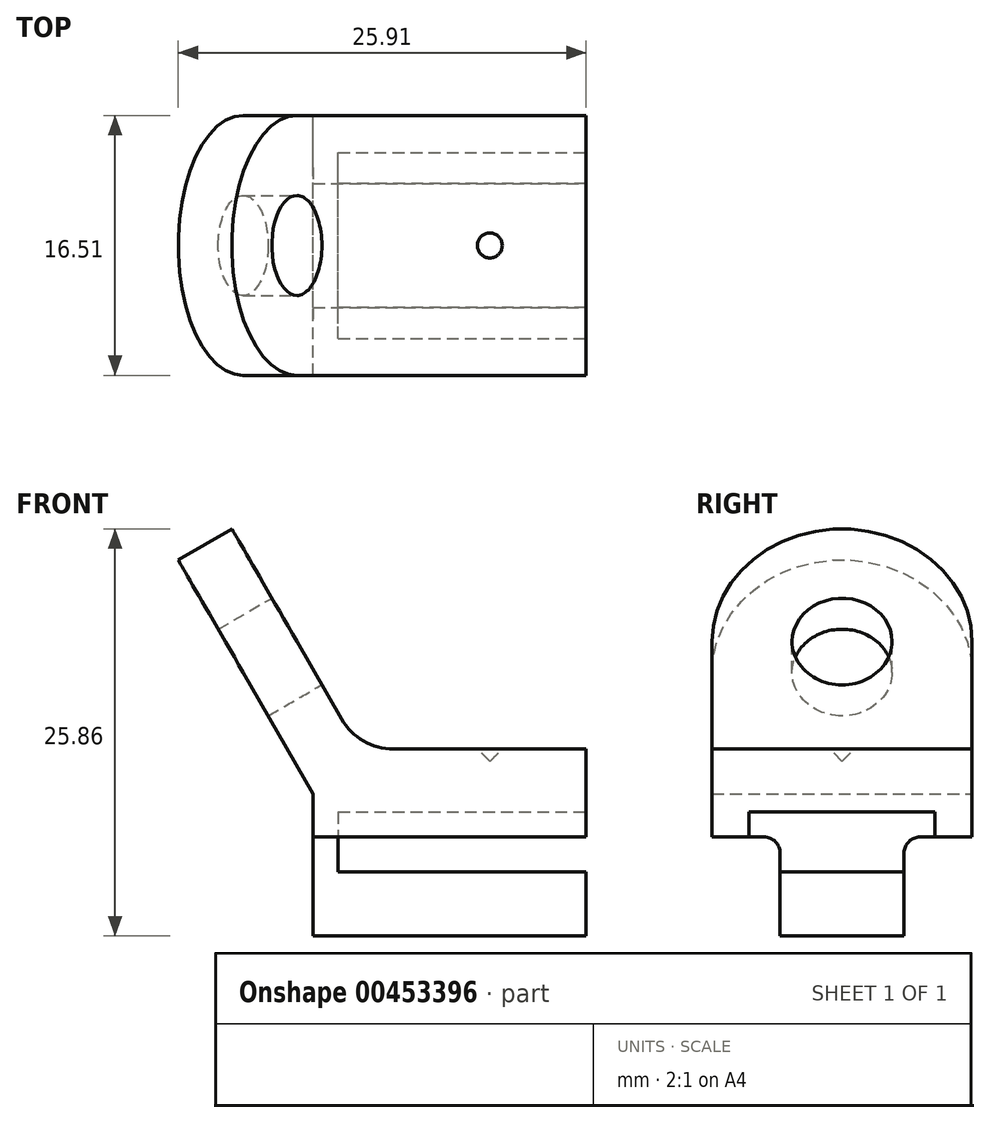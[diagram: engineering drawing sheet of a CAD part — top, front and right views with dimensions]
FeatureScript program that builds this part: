
annotation { "Feature Type Name" : "Feature", "Feature Type Description" : "" }
export const myFeature = defineFeature(function(context is Context, id is Id, definition is map)
    precondition{}
    {
        {
            var Q0;
            Q0=qCreatedBy(makeId("Front.planeOp"),FACE);
            var sketch = newSketch(context, id + "F0", { "sketchPlane" : qUnion([Q0])});
            skLineSegment(sketch, "E0", {"start": v(15.75, 0) * mm, "end": v(0, 0) * mm});
            skLineSegment(sketch, "E1", {"start": v(0, 0) * mm, "end": v(-10.16, 17.6) * mm});
            skLineSegment(sketch, "E2.0", {"start": v(1.32, 5.59) * mm, "end": v(-6.75, 19.57) * mm});
            skLineSegment(sketch, "E3", {"start": v(-10.16, 17.6) * mm, "end": v(-6.75, 19.57) * mm});
            skLineSegment(sketch, "E4", {"start": v(15.75, 5.59) * mm, "end": v(15.75, 0) * mm});
            skLineSegment(sketch, "E5", {"start": v(15.75, 5.59) * mm, "end": v(1.32, 5.59) * mm});
            skSolve(sketch);
        }
        {
            var Q0;
            Q0=makeQuery(id+"F0.imprint","IMPRINT",FACE,{"disambiguationData":[TD([[makeQuery(id+"F0.imprint","IMPRINT",EDGE,{"derivedFrom":sQuery(id+"F0.wireOp",EDGE,"E0")}),-1.0]])]});
            extrude(context, id + "F1", {"entities" : qUnion([Q0]), "depth" : 16.5 * mm});
        }
        {
            var Q0;
            Q0=makeQuery(id+"F1.opExtrude","SWEPT_FACE",FACE,{"disambiguationData":[OSD([sQuery(id+"F0.wireOp",EDGE,"E4")])]});
            var sketch = newSketch(context, id + "F2", { "sketchPlane" : qUnion([Q0])});
            skLineSegment(sketch, "E6.bottom", {"start": v(-2.35, 0) * mm, "end": v(-14.16, 0) * mm});
            skLineSegment(sketch, "E6.top", {"start": v(-2.35, 1.59) * mm, "end": v(-14.16, 1.59) * mm});
            skLineSegment(sketch, "E6.left", {"start": v(-2.35, 0) * mm, "end": v(-2.35, 1.59) * mm});
            skLineSegment(sketch, "E6.right", {"start": v(-14.16, 0) * mm, "end": v(-14.16, 1.59) * mm});
            skPoint(sketch, "E6.middle", {"position": v(-8.26, 0.8) * mm});
            skSolve(sketch);
        }
        {
            var Q0;
            Q0 = qSketchRegion(id + "F2", true);
            extrude(context, id + "F3", {"entities" : qUnion([Q0]), "operationType" : NewBodyOperationType.REMOVE, "endBound" : BoundingType.THROUGH_ALL, "oppositeDirection" : true, "depth" : 12.7 * mm});
        }
        {
            var Q0;
            Q0=makeQuery(id+"F2.imprint","IMPRINT",FACE,{"disambiguationData":[TD([[makeQuery(id+"F2.imprint","IMPRINT",EDGE,{"derivedFrom":sQuery(id+"F2.wireOp",EDGE,"E6.bottom")}),1.0]])]});
            extrude(context, id + "F4", {"entities" : qUnion([Q0]), "operationType" : NewBodyOperationType.REMOVE, "endBound" : BoundingType.THROUGH_ALL, "oppositeDirection" : true, "depth" : 25.4 * mm});
        }
        {
            var Q0;
            Q0=makeQuery(id+"F1.opExtrude","SWEPT_FACE",FACE,{"disambiguationData":[OSD([sQuery(id+"F0.wireOp",EDGE,"E2.0")])]});
            var sketch = newSketch(context, id + "F5", { "sketchPlane" : qUnion([Q0])});
            skCircle(sketch, "E7", {"center": v(-8.26, 12.06) * mm, "radius": 3.18 * mm});
            skSolve(sketch);
        }
        {
            var Q0;
            Q0=makeQuery(id+"F5.imprint","IMPRINT",FACE,{"disambiguationData":[TD([[makeQuery(id+"F5.imprint","IMPRINT",EDGE,{"derivedFrom":sQuery(id+"F5.wireOp",EDGE,"E7")}),1.0]])]});
            extrude(context, id + "F6", {"entities" : qUnion([Q0]), "operationType" : NewBodyOperationType.REMOVE, "endBound" : BoundingType.THROUGH_ALL, "oppositeDirection" : true, "depth" : 25.4 * mm});
        }
        {
            var Q0;
            Q0=makeQuery(id+"F1.opExtrude","CAP_FACE",FACE,{"disambiguationData":[OSD([sQuery(id+"F0.wireOp",EDGE,"E0"),sQuery(id+"F0.wireOp",EDGE,"E1"),sQuery(id+"F0.wireOp",EDGE,"E2.0"),sQuery(id+"F0.wireOp",EDGE,"E3"),sQuery(id+"F0.wireOp",EDGE,"E4"),sQuery(id+"F0.wireOp",EDGE,"E5")])],"isStart":false});
            var Q1;
            Q1=makeQuery(id+"F1.opExtrude","CAP_FACE",FACE,{"disambiguationData":[OSD([sQuery(id+"F0.wireOp",EDGE,"E0"),sQuery(id+"F0.wireOp",EDGE,"E1"),sQuery(id+"F0.wireOp",EDGE,"E2.0"),sQuery(id+"F0.wireOp",EDGE,"E3"),sQuery(id+"F0.wireOp",EDGE,"E4"),sQuery(id+"F0.wireOp",EDGE,"E5")])],"isStart":true});
            cPlane(context, id + "F7", {"entities" : qUnion([Q0, Q1]), "cplaneType" : CPlaneType.MID_PLANE, "offset" : 25.4 * mm, "width" : 152.4 * mm, "height" : 152.4 * mm});
        }
        {
            var Q0;
            Q0=qCreatedBy(id+"F7.planeOp",FACE);
            var sketch = newSketch(context, id + "F8", { "sketchPlane" : qUnion([Q0])});
            skLineSegment(sketch, "E8.0.0", {"start": v(0, 0) * mm, "end": v(-6.47, 11.2) * mm});
            skLineSegment(sketch, "E8.0.1", {"start": v(-6.47, 11.2) * mm, "end": v(-3.06, 13.17) * mm});
            skLineSegment(sketch, "E8.0.2", {"start": v(-3.06, 13.17) * mm, "end": v(1.32, 5.59) * mm});
            skLineSegment(sketch, "E8.0.3", {"start": v(1.32, 5.59) * mm, "end": v(15.75, 5.59) * mm});
            skLineSegment(sketch, "E8.0.4", {"start": v(15.75, 5.59) * mm, "end": v(15.75, 0) * mm});
            skLineSegment(sketch, "E8.0.5", {"start": v(15.75, 0) * mm, "end": v(0, 0) * mm});
            skLineSegment(sketch, "E9", {"start": v(-1.59, 2.75) * mm, "end": v(-1.59, -6.29) * mm});
            skLineSegment(sketch, "E10", {"start": v(-1.59, -6.29) * mm, "end": v(15.75, -6.29) * mm});
            skLineSegment(sketch, "E11", {"start": v(15.75, -6.29) * mm, "end": v(15.75, -2.22) * mm});
            skLineSegment(sketch, "E12", {"start": v(15.75, -2.22) * mm, "end": v(0, -2.22) * mm});
            skLineSegment(sketch, "E13", {"start": v(0, -2.22) * mm, "end": v(0, 0) * mm});
            skLineSegment(sketch, "E14.0", {"start": v(-0.92, 1.59) * mm, "end": v(15.75, 1.59) * mm});
            skSolve(sketch);
        }
        {
            var Q0;
            {var subQ0=sQuery(id+"F8.wireOp",EDGE,"E9");Q0=makeQuery(id+"F8.imprint","IMPRINT",FACE,{"disambiguationData":[TD([[makeQuery(id+"F8.imprint","IMPRINT",EDGE,{"derivedFrom":subQ0}),1.0]])]});}
            extrude(context, id + "F9", {"entities" : qUnion([Q0]), "operationType" : NewBodyOperationType.ADD, "endBound" : BoundingType.SYMMETRIC, "depth" : 7.87 * mm});
        }
        {
            var Q0;
            Q0=qCreatedBy(id+"F7.planeOp",FACE);
            var sketch = newSketch(context, id + "F10", { "sketchPlane" : qUnion([Q0])});
            skLineSegment(sketch, "E15.0.1", {"start": v(0, 0) * mm, "end": v(0, -2.22) * mm});
            skLineSegment(sketch, "E15.0.2", {"start": v(0, -2.22) * mm, "end": v(15.75, -2.22) * mm});
            skLineSegment(sketch, "E15.0.3", {"start": v(15.75, -2.22) * mm, "end": v(15.75, -6.29) * mm});
            skLineSegment(sketch, "E15.0.4", {"start": v(15.75, -6.29) * mm, "end": v(-1.59, -6.29) * mm});
            skLineSegment(sketch, "E15.0.5", {"start": v(-1.59, -6.29) * mm, "end": v(-1.59, 2.75) * mm});
            skLineSegment(sketch, "E15.0.6", {"start": v(-1.59, 2.75) * mm, "end": v(-0.92, 1.59) * mm});
            skLineSegment(sketch, "E16", {"start": v(0, 0) * mm, "end": v(-1.59, 0) * mm});
            skLineSegment(sketch, "E17", {"start": v(-0.92, 1.59) * mm, "end": v(0, 1.59) * mm});
            skLineSegment(sketch, "E18", {"start": v(0, 1.59) * mm, "end": v(0, 0) * mm});
            skSolve(sketch);
        }
        {
            var Q0;
            {var subQ1=sQuery(id+"F10.wireOp",EDGE,"E15.0.6");Q0=makeQuery(id+"F10.imprint","IMPRINT",FACE,{"disambiguationData":[TD([[makeQuery(id+"F10.imprint","IMPRINT",EDGE,{"derivedFrom":subQ1}),-1.0]])]});}
            extrude(context, id + "F11", {"entities" : qUnion([Q0]), "operationType" : NewBodyOperationType.ADD, "endBound" : BoundingType.SYMMETRIC, "depth" : 16.5 * mm});
        }
        {
            var Q0;
            Q0=makeQuery(id+"F11.boolean.opBoolean","INTERSECT",EDGE,{"derivedFrom":[makeQuery(id+"F9.opExtrude","CAP_FACE",FACE,{"disambiguationData":[OSD([sQuery(id+"F8.wireOp",EDGE,"E8.0.0"),sQuery(id+"F8.wireOp",EDGE,"E9"),sQuery(id+"F8.wireOp",EDGE,"E10"),sQuery(id+"F8.wireOp",EDGE,"E11"),sQuery(id+"F8.wireOp",EDGE,"E12"),sQuery(id+"F8.wireOp",EDGE,"E13")])],"isStart":true}),makeQuery(id+"F11.opExtrude","SWEPT_FACE",FACE,{"disambiguationData":[OSD([sQuery(id+"F10.wireOp",EDGE,"E16")])]})]});
            var Q1;
            Q1=makeQuery(id+"F11.boolean.opBoolean","INTERSECT",EDGE,{"derivedFrom":[makeQuery(id+"F9.opExtrude","CAP_FACE",FACE,{"disambiguationData":[OSD([sQuery(id+"F8.wireOp",EDGE,"E8.0.0"),sQuery(id+"F8.wireOp",EDGE,"E9"),sQuery(id+"F8.wireOp",EDGE,"E10"),sQuery(id+"F8.wireOp",EDGE,"E11"),sQuery(id+"F8.wireOp",EDGE,"E12"),sQuery(id+"F8.wireOp",EDGE,"E13")])],"isStart":false}),makeQuery(id+"F11.opExtrude","SWEPT_FACE",FACE,{"disambiguationData":[OSD([sQuery(id+"F10.wireOp",EDGE,"E16")])]})]});
            fillet(context, id + "F12", {"entities" : qUnion([Q0, Q1]), "radius" : 1.02 * mm, "tangentPropagation" : true, "allowEdgeOverflow" : false});
        }
        {
            var Q0;
            Q0=makeQuery(id+"F11.boolean.opBoolean","MERGE",EDGE,{"derivedFrom":[makeQuery(id+"F9.opExtrude","SWEPT_EDGE",EDGE,{"disambiguationData":[OSD([sQuery(id+"F8.wireOp",EDGE,"E8.0.0"),sQuery(id+"F8.wireOp",EDGE,"E9")])]}),makeQuery(id+"F11.opExtrude","SWEPT_EDGE",EDGE,{"disambiguationData":[OSD([sQuery(id+"F10.wireOp",EDGE,"E15.0.5"),sQuery(id+"F10.wireOp",EDGE,"E15.0.6")])]})]});
            var Q1;
            Q1=makeQuery(id+"F1.opExtrude","SWEPT_EDGE",EDGE,{"disambiguationData":[OSD([sQuery(id+"F0.wireOp",EDGE,"E2.0"),sQuery(id+"F0.wireOp",EDGE,"E5")])]});
            fillet(context, id + "F13", {"entities" : qUnion([Q0, Q1]), "radius" : 3.8 * mm, "tangentPropagation" : true, "allowEdgeOverflow" : false});
        }
        {
            var Q0;
            Q0=makeQuery(id+"F11.boolean.opBoolean","MERGE",FACE,{"derivedFrom":[makeQuery(id+"F1.opExtrude","CAP_FACE",FACE,{"disambiguationData":[OSD([sQuery(id+"F0.wireOp",EDGE,"E0"),sQuery(id+"F0.wireOp",EDGE,"E1"),sQuery(id+"F0.wireOp",EDGE,"E2.0"),sQuery(id+"F0.wireOp",EDGE,"E3"),sQuery(id+"F0.wireOp",EDGE,"E4"),sQuery(id+"F0.wireOp",EDGE,"E5")])],"isStart":false}),makeQuery(id+"F11.opExtrude","CAP_FACE",FACE,{"disambiguationData":[OSD([sQuery(id+"F10.wireOp",EDGE,"E15.0.5"),sQuery(id+"F10.wireOp",EDGE,"E15.0.6"),sQuery(id+"F10.wireOp",EDGE,"E16"),sQuery(id+"F10.wireOp",EDGE,"E17"),sQuery(id+"F10.wireOp",EDGE,"E18")])],"isStart":false})]});
            var Q1;
            Q1=makeQuery(id+"F11.boolean.opBoolean","MERGE",FACE,{"derivedFrom":[makeQuery(id+"F1.opExtrude","CAP_FACE",FACE,{"disambiguationData":[OSD([sQuery(id+"F0.wireOp",EDGE,"E0"),sQuery(id+"F0.wireOp",EDGE,"E1"),sQuery(id+"F0.wireOp",EDGE,"E2.0"),sQuery(id+"F0.wireOp",EDGE,"E3"),sQuery(id+"F0.wireOp",EDGE,"E4"),sQuery(id+"F0.wireOp",EDGE,"E5")])],"isStart":true}),makeQuery(id+"F11.opExtrude","CAP_FACE",FACE,{"disambiguationData":[OSD([sQuery(id+"F10.wireOp",EDGE,"E15.0.5"),sQuery(id+"F10.wireOp",EDGE,"E15.0.6"),sQuery(id+"F10.wireOp",EDGE,"E16"),sQuery(id+"F10.wireOp",EDGE,"E17"),sQuery(id+"F10.wireOp",EDGE,"E18")])],"isStart":true})]});
            cPlane(context, id + "F14", {"entities" : qUnion([Q0, Q1]), "cplaneType" : CPlaneType.MID_PLANE, "offset" : 25.4 * mm, "width" : 152.4 * mm, "height" : 152.4 * mm});
        }
        {
            var Q0;
            Q0=qCreatedBy(id+"F14.planeOp",FACE);
            var sketch = newSketch(context, id + "F15", { "sketchPlane" : qUnion([Q0])});
            skLineSegment(sketch, "E19.0.0", {"start": v(-1.59, 0) * mm, "end": v(-1.59, 1.73) * mm});
            skArc(sketch, "E19.0.1", {"start": v(-1.59, 1.73) * mm, "mid": v(-1.72, 2.71) * mm, "end": v(-2.1, 3.63) * mm});
            skLineSegment(sketch, "E19.0.2", {"start": v(-2.1, 3.63) * mm, "end": v(-6.35, 11) * mm});
            skLineSegment(sketch, "E19.0.3", {"start": v(-6.35, 11) * mm, "end": v(-2.94, 12.97) * mm});
            skLineSegment(sketch, "E19.0.4", {"start": v(-2.94, 12.97) * mm, "end": v(0.22, 7.5) * mm});
            skArc(sketch, "E19.0.5", {"start": v(0.22, 7.5) * mm, "mid": v(1.61, 6.1) * mm, "end": v(3.52, 5.59) * mm});
            skLineSegment(sketch, "E19.0.6", {"start": v(3.52, 5.59) * mm, "end": v(15.75, 5.59) * mm});
            skLineSegment(sketch, "E19.0.7", {"start": v(15.75, 5.59) * mm, "end": v(15.75, 0) * mm});
            skLineSegment(sketch, "E19.0.8", {"start": v(15.75, 0) * mm, "end": v(-1.59, 0) * mm});
            skLineSegment(sketch, "E20", {"start": v(9.63, 5.59) * mm, "end": v(9.63, 4.8) * mm});
            skLineSegment(sketch, "E21", {"start": v(9.63, 4.8) * mm, "end": v(8.84, 5.59) * mm});
            skLineSegment(sketch, "E22", {"start": v(8.84, 5.59) * mm, "end": v(9.63, 5.59) * mm});
            skSolve(sketch);
        }
        {
            var Q0;
            Q0=makeQuery(id+"F15.imprint","IMPRINT",FACE,{"disambiguationData":[TD([[makeQuery(id+"F15.imprint","IMPRINT",EDGE,{"derivedFrom":sQuery(id+"F15.wireOp",EDGE,"E20")}),-1.0]])]});
            var Q1;
            Q1=sQuery(id+"F15.wireOp",EDGE,"E20");
            revolve(context, id + "F16", {"operationType" : NewBodyOperationType.REMOVE, "entities" : qUnion([Q0]), "axis" : qUnion([Q1]), "revolveType" : RevolveType.FULL, "oppositeDirection" : true});
        }
        {
            var Q0;
            Q0=makeQuery(id+"F1.opExtrude","SWEPT_FACE",FACE,{"disambiguationData":[OSD([sQuery(id+"F0.wireOp",EDGE,"E2.0")])]});
            var sketch = newSketch(context, id + "F17", { "sketchPlane" : qUnion([Q0])});
            skCircle(sketch, "E23.0", {"center": v(-8.26, 12.06) * mm, "radius": 3.18 * mm});
            skArc(sketch, "E24", {"start": v(-16.51, 12.06) * mm, "mid": v(-8.26, 20.32) * mm, "end": v(0, 12.06) * mm});
            skLineSegment(sketch, "E25", {"start": v(-16.51, 12.06) * mm, "end": v(-16.51, 20.32) * mm});
            skLineSegment(sketch, "E26", {"start": v(-16.51, 20.32) * mm, "end": v(0, 20.32) * mm});
            skLineSegment(sketch, "E27", {"start": v(0, 20.32) * mm, "end": v(0, 12.06) * mm});
            skSolve(sketch);
        }
        {
            var Q0;
            {var subQ0=sQuery(id+"F17.wireOp",EDGE,"E25");Q0=makeQuery(id+"F17.imprint","IMPRINT",FACE,{"disambiguationData":[TD([[makeQuery(id+"F17.imprint","IMPRINT",EDGE,{"derivedFrom":subQ0}),-1.0]])]});}
            var Q1;
            {var subQ0=sQuery(id+"F17.wireOp",EDGE,"E27");Q1=makeQuery(id+"F17.imprint","IMPRINT",FACE,{"disambiguationData":[TD([[makeQuery(id+"F17.imprint","IMPRINT",EDGE,{"derivedFrom":subQ0}),1.0]])]});}
            extrude(context, id + "F18", {"entities" : qUnion([Q0, Q1]), "operationType" : NewBodyOperationType.REMOVE, "oppositeDirection" : true, "depth" : 25.4 * mm});
        }
    });
